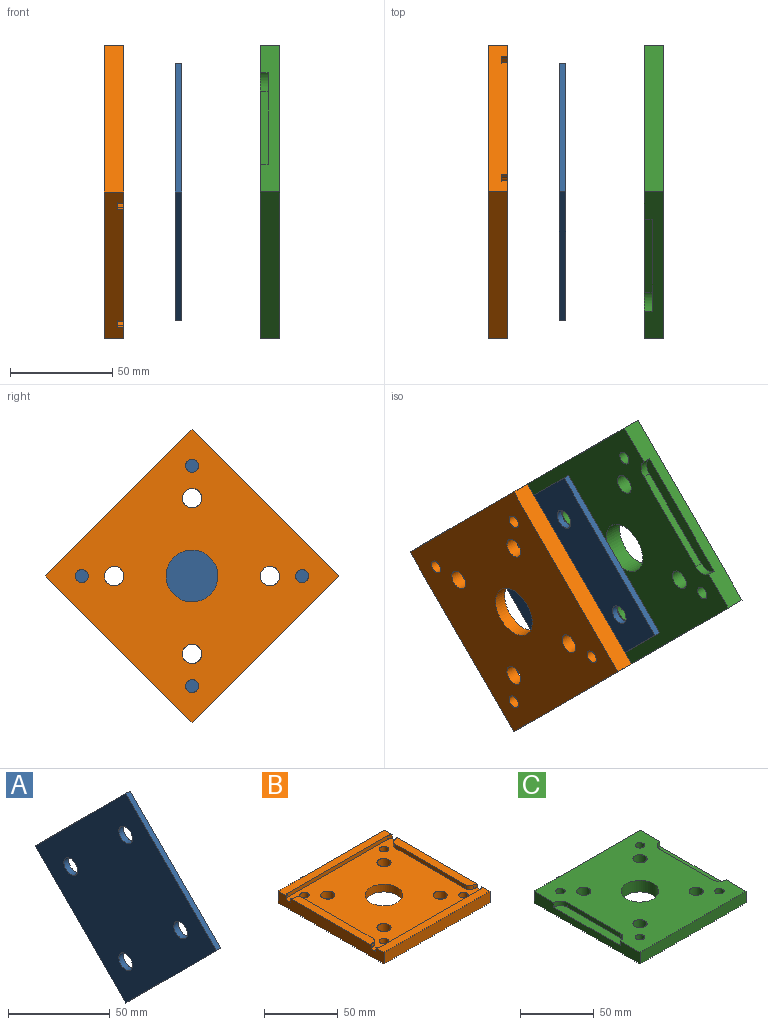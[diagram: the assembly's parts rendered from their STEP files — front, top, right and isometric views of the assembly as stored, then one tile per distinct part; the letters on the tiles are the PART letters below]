
ASSEMBLY  parts=3 mates=4
PART A: 10 faces, bbox 3.2x125.7x125.7 mm
  f0: plane 62.86x62.86mm, normal (0,0.71,-0.71), area 282.3mm2, adj f1,f6,f8,f9
  f1: plane 62.86x62.86mm, normal (0,0.71,0.71), area 282.3mm2, adj f0,f2,f8,f9
  f2: plane 62.86x62.86mm, normal (0,-0.71,0.71), area 282.3mm2, adj f1,f6,f8,f9
  f3: cylinder r=4.76mm len=9.53mm, axis (-1,0,0), area 95mm2, adj f8,f9
  f4: cylinder r=4.76mm len=9.53mm, axis (-1,0,0), area 95mm2, adj f8,f9
  f5: cylinder r=4.76mm len=9.53mm, axis (-1,0,0), area 95mm2, adj f8,f9
  f6: plane 62.86x62.86mm, normal (0,-0.71,-0.71), area 282.3mm2, adj f0,f2,f8,f9
  f7: cylinder r=4.76mm len=9.53mm, axis (-1,0,0), area 95mm2, adj f8,f9
  f8: plane 125.72x125.72mm, normal (1,0,0), area 7618.2mm2, adj f0,f1,f2,f3,f4,f5,f6,f7
  f9: plane 125.72x125.72mm, normal (-1,0,0), area 7618.2mm2, adj f0,f1,f2,f3,f4,f5,f6,f7
PART B: 35 faces, bbox 101.6x101.6x9.5 mm
  f0: plane 101.6x7.83mm, normal (0,0,1), area 647.7mm2, adj f3,f8,f9,f11,f19,f20
  f1: plane 101.6x7.83mm, normal (0,0,1), area 647.7mm2, adj f3,f7,f8,f12,f14,f25
  f2: plane 77.9x6.35mm, normal (0,0,1), area 473.1mm2, adj f5,f8,f15,f16,f17,f18
  f3: plane 101.6x9.53mm, normal (-1,0,0), area 942.2mm2, adj f0,f1,f6,f7,f9,f10,f13,f20
  f4: plane 67.95x3.18mm, normal (1,0,0), area 215.7mm2, adj f6,f13,f22,f23
  f5: plane 67.95x3.18mm, normal (-1,0,0), area 215.7mm2, adj f2,f13,f16,f17
  f6: plane 77.9x6.35mm, normal (0,0,1), area 473.1mm2, adj f3,f4,f21,f22,f23,f24
  f7: plane 101.6x9.53mm, normal (0,-1,0), area 967.7mm2, adj f1,f3,f8,f10
  f8: plane 101.6x9.53mm, normal (1,0,0), area 942.2mm2, adj f0,f1,f2,f7,f9,f10,f13,f14
  f9: plane 101.6x9.53mm, normal (0,1,0), area 967.7mm2, adj f0,f3,f8,f10
  f10: plane 101.6x101.6mm, normal (0,0,-1), area 9404.2mm2, adj f3,f7,f8,f9,f26,f27,f28,f29
  f11: plane 95.89x3.18mm, normal (0,-1,0), area 304.4mm2, adj f0,f13,f19,f20
  f12: plane 95.89x3.18mm, normal (0,1,0), area 304.4mm2, adj f1,f13,f14,f25
  f13: plane 101.6x88.9mm, normal (0,0,1), area 7162.6mm2, adj f3,f4,f5,f8,f11,f12,f14,f15
  f14: cylinder r=3.49mm len=3.18mm, axis (0,0,1), area 10.6mm2, adj f1,f8,f12,f13
  f15: cylinder r=3.49mm len=3.18mm, axis (0,0,1), area 10.6mm2, adj f2,f8,f13,f16
  f16: cylinder r=3.49mm len=3.49mm, axis (0,0,1), area 17.4mm2, adj f2,f5,f13,f15
  f17: cylinder r=3.49mm len=3.49mm, axis (0,0,1), area 17.4mm2, adj f2,f5,f13,f18
  f18: cylinder r=3.49mm len=3.18mm, axis (0,0,1), area 10.6mm2, adj f2,f8,f13,f17
  f19: cylinder r=3.49mm len=3.18mm, axis (0,0,1), area 10.6mm2, adj f0,f8,f11,f13
  f20: cylinder r=3.49mm len=3.18mm, axis (0,0,1), area 10.6mm2, adj f0,f3,f11,f13
  f21: cylinder r=3.49mm len=3.18mm, axis (0,0,1), area 10.6mm2, adj f3,f6,f13,f22
  f22: cylinder r=3.49mm len=3.49mm, axis (0,0,1), area 17.4mm2, adj f4,f6,f13,f21
  f23: cylinder r=3.49mm len=3.49mm, axis (0,0,1), area 17.4mm2, adj f4,f6,f13,f24
  f24: cylinder r=3.49mm len=3.18mm, axis (0,0,1), area 10.6mm2, adj f3,f6,f13,f23
  f25: cylinder r=3.49mm len=3.18mm, axis (0,0,1), area 10.6mm2, adj f1,f3,f12,f13
  f26: cylinder r=4.76mm len=9.53mm, axis (0,0,1), area 190mm2, adj f10,f13
  f27: cylinder r=4.76mm len=9.53mm, axis (0,0,1), area 190mm2, adj f10,f13
  f28: cylinder r=4.76mm len=9.53mm, axis (0,0,1), area 190mm2, adj f10,f13
  f29: cylinder r=4.76mm len=9.53mm, axis (0,0,1), area 190mm2, adj f10,f13
  f30: cylinder r=12.7mm len=25.4mm, axis (0,0,1), area 506.7mm2, adj f10,f13
  f31: cylinder r=3.17mm len=6.35mm, axis (0,0,1), area 126.7mm2, adj f10,f13
  f32: cylinder r=3.17mm len=6.35mm, axis (0,0,1), area 126.7mm2, adj f10,f13
  f33: cylinder r=3.17mm len=6.35mm, axis (0,0,1), area 126.7mm2, adj f10,f13
  f34: cylinder r=3.17mm len=6.35mm, axis (0,0,1), area 126.7mm2, adj f10,f13
PART C: 23 faces, bbox 101.6x101.6x9.5 mm
  f0: plane 101.6x9.53mm, normal (-1,0,0), area 725.8mm2, adj f1,f11,f13,f14,f19,f21,f22
  f1: plane 101.6x9.53mm, normal (0,-1,0), area 967.7mm2, adj f0,f2,f13,f14
  f2: plane 101.6x9.53mm, normal (1,0,0), area 725.8mm2, adj f1,f11,f13,f14,f15,f17,f18
  f3: cylinder r=3.17mm len=9.53mm, axis (0,0,-1), area 190mm2, adj f13,f14
  f4: cylinder r=3.17mm len=9.53mm, axis (0,0,-1), area 190mm2, adj f13,f14
  f5: cylinder r=3.17mm len=9.53mm, axis (0,0,-1), area 190mm2, adj f13,f14
  f6: cylinder r=12.7mm len=25.4mm, axis (0,0,-1), area 760.1mm2, adj f13,f14
  f7: cylinder r=4.76mm len=9.53mm, axis (0,0,-1), area 285mm2, adj f13,f14
  f8: cylinder r=4.76mm len=9.53mm, axis (0,0,-1), area 285mm2, adj f13,f14
  f9: cylinder r=4.76mm len=9.53mm, axis (0,0,-1), area 285mm2, adj f13,f14
  f10: cylinder r=4.76mm len=9.53mm, axis (0,0,-1), area 285mm2, adj f13,f14
  f11: plane 101.6x9.53mm, normal (0,1,0), area 967.7mm2, adj f0,f2,f13,f14
  f12: cylinder r=3.17mm len=9.53mm, axis (0,0,-1), area 190mm2, adj f13,f14
  f13: plane 101.6x101.6mm, normal (0,0,1), area 8632.3mm2, adj f0,f1,f2,f3,f4,f5,f6,f7
  f14: plane 101.6x101.6mm, normal (0,0,-1), area 9404.2mm2, adj f0,f1,f2,f3,f4,f5,f6,f7
  f15: cylinder r=6.35mm len=6.35mm, axis (0,0,1), area 38mm2, adj f2,f13,f16,f18
  f16: plane 50.8x3.81mm, normal (1,0,0), area 193.5mm2, adj f13,f15,f17,f18
  f17: cylinder r=6.35mm len=6.35mm, axis (0,0,1), area 38mm2, adj f2,f13,f16,f18
  f18: plane 63.5x6.35mm, normal (0,0,1), area 385.9mm2, adj f2,f15,f16,f17
  f19: cylinder r=6.35mm len=6.35mm, axis (0,0,1), area 38mm2, adj f0,f13,f20,f22
  f20: plane 50.8x3.81mm, normal (-1,0,0), area 193.5mm2, adj f13,f19,f21,f22
  f21: cylinder r=6.35mm len=6.35mm, axis (0,0,1), area 38mm2, adj f0,f13,f20,f22
  f22: plane 63.5x6.35mm, normal (0,0,1), area 385.9mm2, adj f0,f19,f20,f21
PLACE A at identity fixed
PLACE B rot(axis=(0.68,0.28,0.68),148.6deg) t=(9.51,-747.74,359.82)mm
PLACE C rot(axis=(0.36,-0.86,-0.36),98.4deg) t=(95.5,-747.74,359.82)mm
MATE cylindrical C.f8 <-> A.f5  axis (1,0,0) through (95.5,-747.74,393.56)mm
MATE cylindrical B.f29 <-> A.f5  axis (1,0,0) through (15.86,-747.74,393.56)mm
MATE cylindrical C.f7 <-> A.f4  axis (1,0,0) through (95.5,-747.74,469.76)mm
MATE cylindrical B.f27 <-> A.f4  axis (1,0,0) through (15.86,-747.74,469.76)mm
